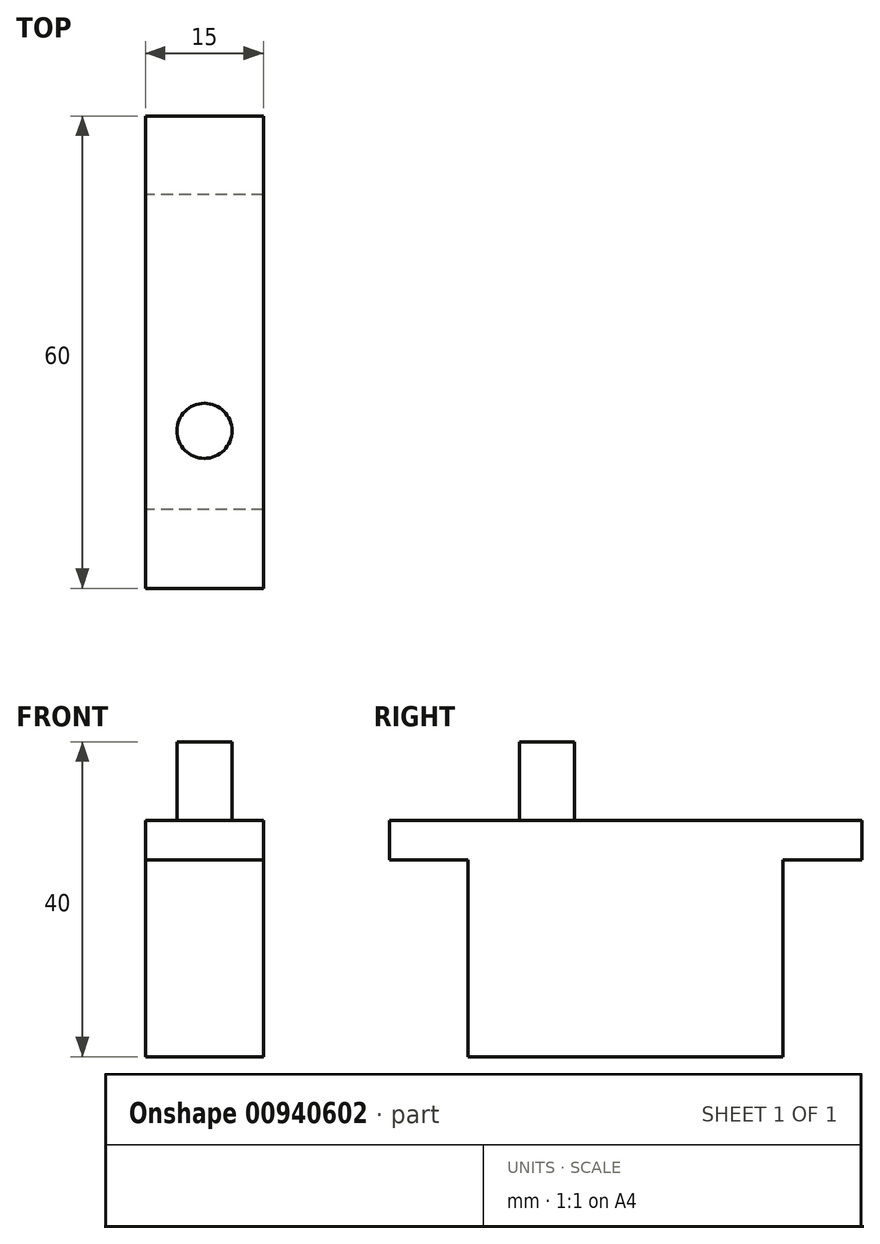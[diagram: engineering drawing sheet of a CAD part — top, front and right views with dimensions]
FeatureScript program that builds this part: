
annotation { "Feature Type Name" : "Feature", "Feature Type Description" : "" }
export const myFeature = defineFeature(function(context is Context, id is Id, definition is map)
    precondition{}
    {
        {
            var Q0;
            Q0=qCreatedBy(makeId("Right.planeOp"),FACE);
            var sketch = newSketch(context, id + "F0", { "sketchPlane" : qUnion([Q0])});
            skLineSegment(sketch, "E0", {"start": v(-23.36, -13.63) * mm, "end": v(-23.36, -38.63) * mm});
            skLineSegment(sketch, "E1", {"start": v(-23.36, -38.63) * mm, "end": v(16.64, -38.63) * mm});
            skLineSegment(sketch, "E2", {"start": v(16.64, -38.63) * mm, "end": v(16.64, -13.63) * mm});
            skLineSegment(sketch, "E3", {"start": v(16.64, -13.63) * mm, "end": v(26.64, -13.63) * mm});
            skLineSegment(sketch, "E4", {"start": v(26.64, -13.63) * mm, "end": v(26.64, -8.63) * mm});
            skLineSegment(sketch, "E5", {"start": v(26.64, -8.63) * mm, "end": v(-33.36, -8.63) * mm});
            skLineSegment(sketch, "E6", {"start": v(-33.36, -8.63) * mm, "end": v(-33.36, -13.63) * mm});
            skLineSegment(sketch, "E7", {"start": v(-33.36, -13.63) * mm, "end": v(-23.36, -13.63) * mm});
            skSolve(sketch);
        }
        {
            var Q0;
            Q0 = qSketchRegion(id + "F0", true);
            extrude(context, id + "F1", {"entities" : qUnion([Q0]), "depth" : 15 * mm, "offsetDistance" : 25 * mm});
        }
        {
            var Q0;
            Q0=makeQuery(id+"F1.opExtrude","SWEPT_FACE",FACE,{"disambiguationData":[OSD([sQuery(id+"F0.wireOp",EDGE,"E5")])]});
            var sketch = newSketch(context, id + "F2", { "sketchPlane" : qUnion([Q0])});
            skCircle(sketch, "E8", {"center": v(7.5, -13.36) * mm, "radius": 3.5 * mm});
            skPoint(sketch, "E8.centerSnap0", {"position": v(7.5, -33.36) * mm});
            skSolve(sketch);
        }
        {
            var Q0;
            Q0 = qSketchRegion(id + "F2", true);
            extrude(context, id + "F3", {"entities" : qUnion([Q0]), "operationType" : NewBodyOperationType.ADD, "depth" : 10 * mm, "offsetDistance" : 25 * mm});
        }
    });
